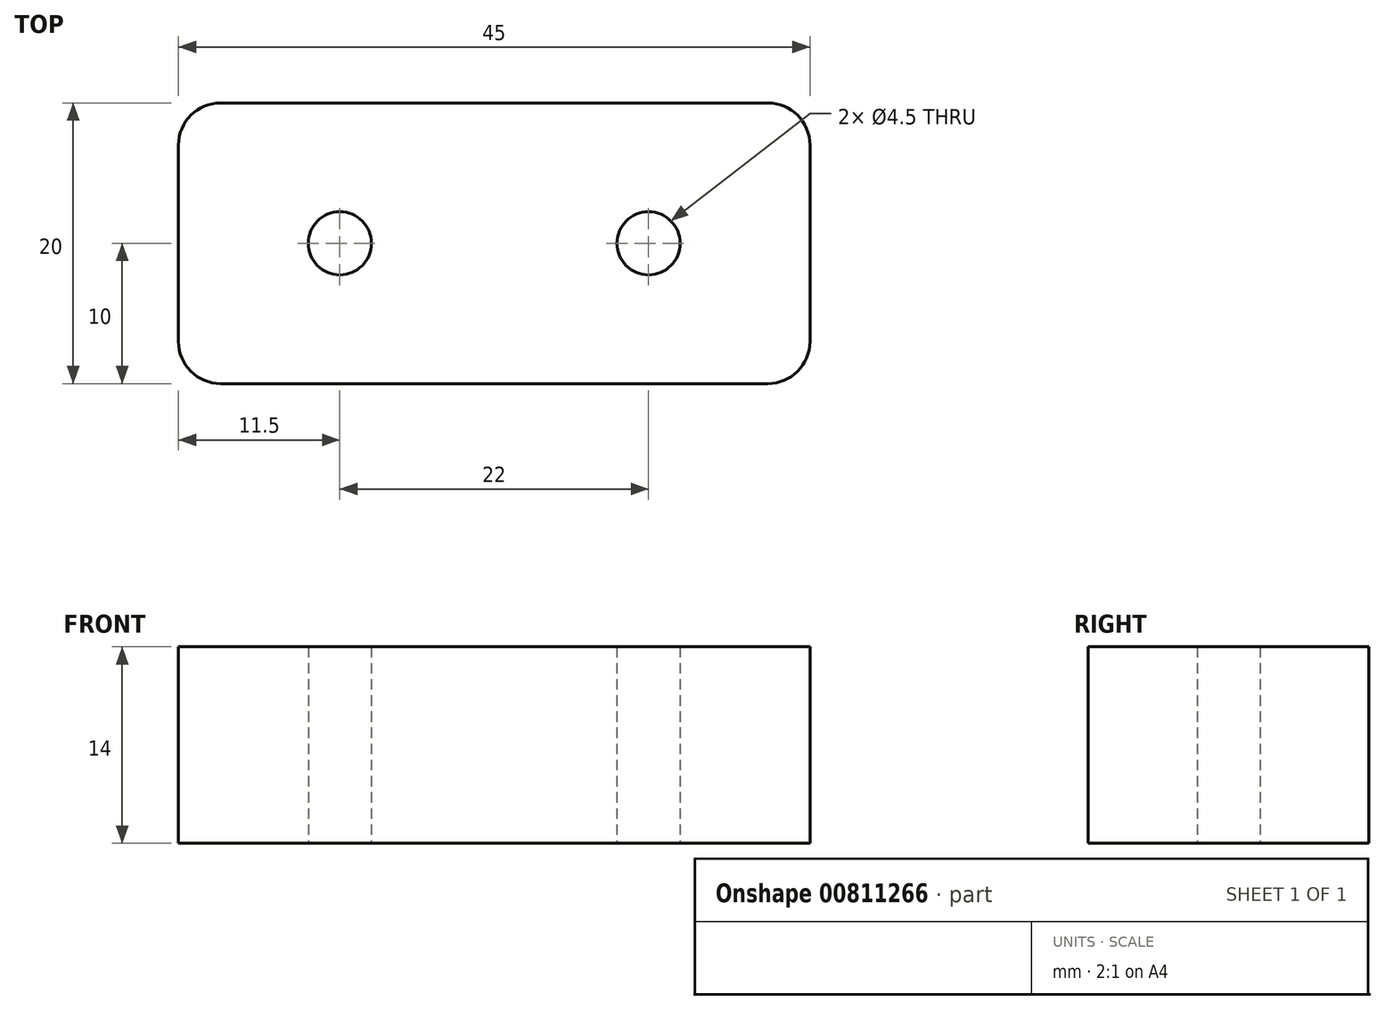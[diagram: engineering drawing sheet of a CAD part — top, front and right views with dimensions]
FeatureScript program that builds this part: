
annotation { "Feature Type Name" : "Feature", "Feature Type Description" : "" }
export const myFeature = defineFeature(function(context is Context, id is Id, definition is map)
    precondition{}
    {
        {
            var Q0;
            Q0=qCreatedBy(makeId("Top.planeOp"),FACE);
            var sketch = newSketch(context, id + "F0", { "sketchPlane" : qUnion([Q0])});
            skLineSegment(sketch, "E0.bottom", {"start": v(22.5, -10) * mm, "end": v(-22.5, -10) * mm});
            skLineSegment(sketch, "E0.top", {"start": v(22.5, 10) * mm, "end": v(-22.5, 10) * mm});
            skLineSegment(sketch, "E0.left", {"start": v(22.5, -10) * mm, "end": v(22.5, 10) * mm});
            skLineSegment(sketch, "E0.right", {"start": v(-22.5, -10) * mm, "end": v(-22.5, 10) * mm});
            skPoint(sketch, "E0.middle", {"position": v(0, 0) * mm});
            skLineSegment(sketch, "E1", {"start": v(0, 0) * mm, "end": v(0, 10) * mm, "construction": true});
            skPoint(sketch, "E2", {"position": v(-11, 0) * mm});
            skPoint(sketch, "E3.MirrorP", {"position": v(11, 0) * mm});
            skCircle(sketch, "E4", {"center": v(-11, 0) * mm, "radius": 2.25 * mm});
            skCircle(sketch, "E5.MirrorC", {"center": v(11, 0) * mm, "radius": 2.25 * mm});
            skSolve(sketch);
        }
        {
            var Q0;
            Q0 = qSketchRegion(id + "F0", true);
            extrude(context, id + "F1", {"entities" : qUnion([Q0]), "depth" : 14 * mm, "offsetDistance" : 25 * mm});
        }
        {
            var Q0;
            Q0=makeQuery(id+"F1.opExtrude","SWEPT_EDGE",EDGE,{"disambiguationData":[OSD([sQuery(id+"F0.wireOp",EDGE,"E0.bottom"),sQuery(id+"F0.wireOp",EDGE,"E0.left")])]});
            var Q1;
            Q1=makeQuery(id+"F1.opExtrude","SWEPT_EDGE",EDGE,{"disambiguationData":[OSD([sQuery(id+"F0.wireOp",EDGE,"E0.top"),sQuery(id+"F0.wireOp",EDGE,"E0.left")])]});
            var Q2;
            Q2=makeQuery(id+"F1.opExtrude","SWEPT_EDGE",EDGE,{"disambiguationData":[OSD([sQuery(id+"F0.wireOp",EDGE,"E0.top"),sQuery(id+"F0.wireOp",EDGE,"E0.right")])]});
            var Q3;
            Q3=makeQuery(id+"F1.opExtrude","SWEPT_EDGE",EDGE,{"disambiguationData":[OSD([sQuery(id+"F0.wireOp",EDGE,"E0.bottom"),sQuery(id+"F0.wireOp",EDGE,"E0.right")])]});
            fillet(context, id + "F2", {"entities" : qUnion([Q0, Q1, Q2, Q3]), "tangentPropagation" : true, "radius" : 3 * mm, "defaultsChanged" : false, "vertexSettings" : [], "allowEdgeOverflow" : false});
        }
    });
